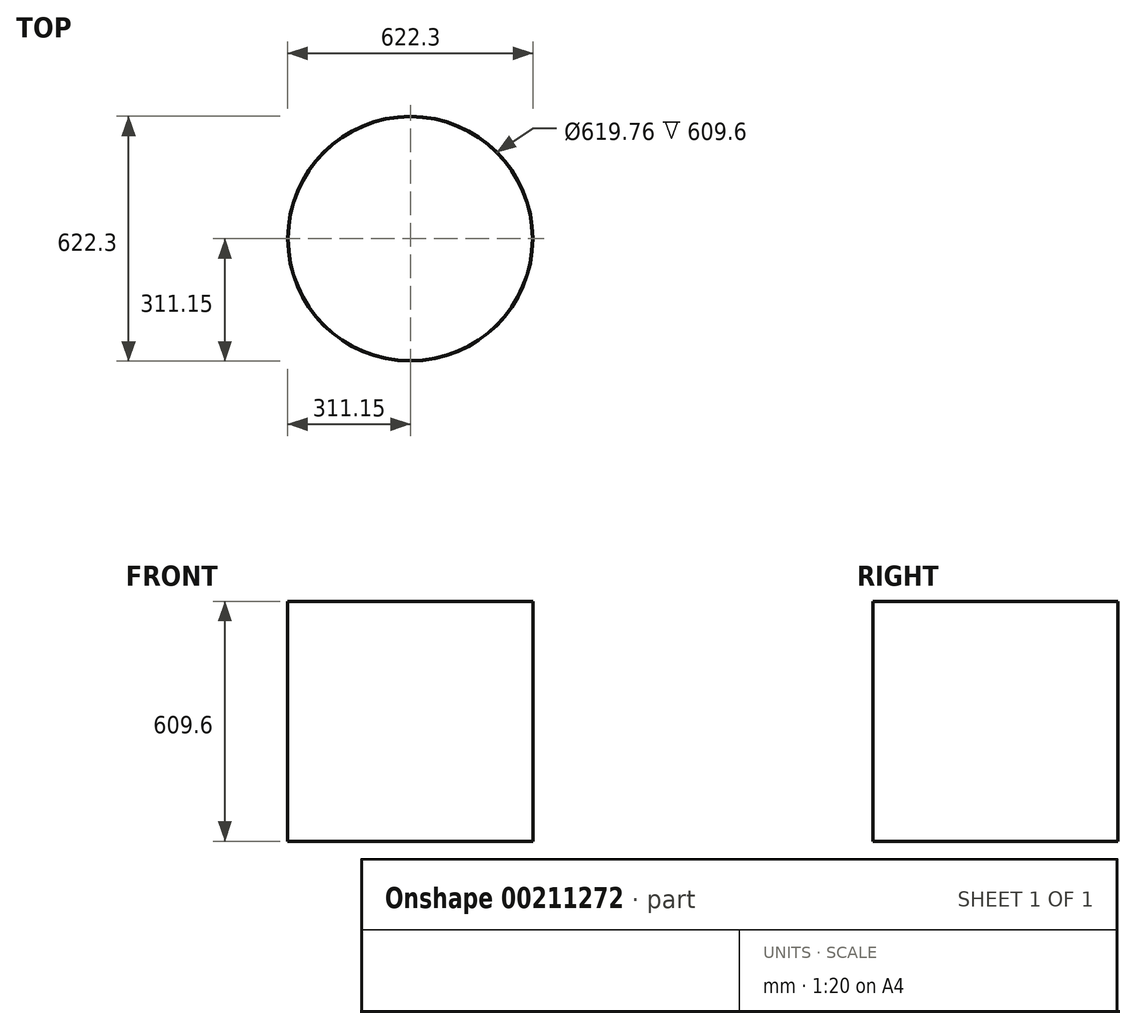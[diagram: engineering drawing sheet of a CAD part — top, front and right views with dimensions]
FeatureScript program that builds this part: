
annotation { "Feature Type Name" : "Feature", "Feature Type Description" : "" }
export const myFeature = defineFeature(function(context is Context, id is Id, definition is map)
    precondition{}
    {
        {
            var Q0;
            Q0=qCreatedBy(makeId("Top.planeOp"),FACE);
            var sketch = newSketch(context, id + "F0", { "sketchPlane" : qUnion([Q0])});
            skCircle(sketch, "E0", {"center": v(0, 0) * mm, "radius": 311.15 * mm});
            skCircle(sketch, "E1", {"center": v(0, 0) * mm, "radius": 309.88 * mm});
            skSolve(sketch);
        }
        {
            var Q0;
            Q0 = qSketchRegion(id + "F0", true);
            extrude(context, id + "F1", {"entities" : qUnion([Q0]), "depth" : 609.6 * mm});
        }
    });
